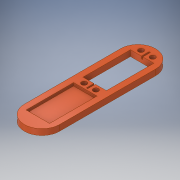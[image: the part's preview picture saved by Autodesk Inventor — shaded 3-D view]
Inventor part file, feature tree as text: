
AUTODESK INVENTOR PART (.ipt)
format: ipt  version: 2017 (Build 210142000, 142)  size: 168,960 bytes
history: native  units: mm
features: extrude x5, sketch x4, fillet x2
ambient origin geometry x8: Origin, YZ Plane, XZ Plane, XY Plane, X Axis, Y Axis, Z Axis, Center Point
bodies: Solid1 (feature_tree)
feature tree (11):
  extrude  "Extrusion1"  Depth=30.0mm
  sketch  "Sketch2"  dims[d2=5.0mm d3=0.0mm]
  extrude  "Extrusion2"  TaperAngle=0.0deg  [1 undecoded]
  extrude  "Extrusion3"  Depth=20.0mm
  extrude  "Extrusion4"  Depth=2.0mm
  extrude  "Extrusion5"  Depth=5.0mm
  fillet  "Fillet1"  [1 undecoded]
  fillet  "Fillet2"  Radius=2.5mm
  sketch  "Sketch1"  dims[d0=30.0mm d1=112.0mm]
  sketch  "Sketch3"  dims[d4=5.0mm d5=20.0mm]
  sketch  "Sketch4"  dims[d6=40.5mm d7=11.5mm d8=5.0mm d9=0.0mm d10=2.5mm d11=0.0mm d13=4.0mm d14=4.0mm d15=2.75mm d16=2.75mm d17=4.5mm d18=2.5mm d19=0.0mm d20=6.5mm d21=1.2mm d22=2.0mm d23=0.0mm]
note: 2 required parameter values undecoded (feature->parameter linkage not recoverable at this tier; creation-order binding heuristic only, values carry confidence <= 0.55)
